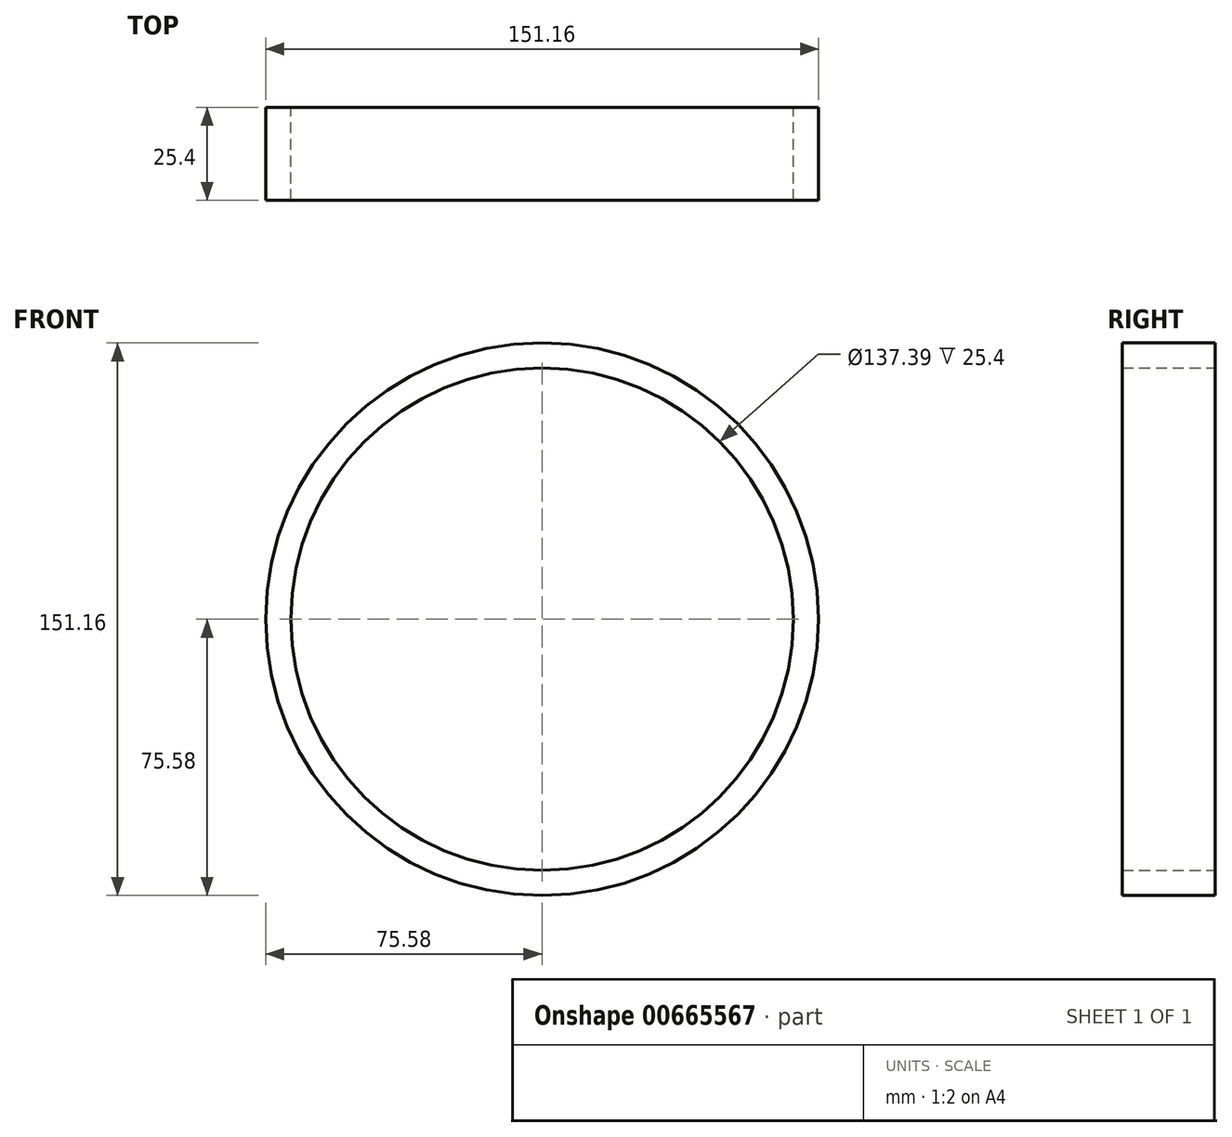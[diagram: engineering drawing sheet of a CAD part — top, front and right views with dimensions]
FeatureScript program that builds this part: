
annotation { "Feature Type Name" : "Feature", "Feature Type Description" : "" }
export const myFeature = defineFeature(function(context is Context, id is Id, definition is map)
    precondition{}
    {
        {
            var Q0;
            Q0=qCreatedBy(makeId("Front.planeOp"),FACE);
            var sketch = newSketch(context, id + "F0", { "sketchPlane" : qUnion([Q0])});
            skCircle(sketch, "E0", {"center": v(0, 0) * mm, "radius": 75.58 * mm});
            skSolve(sketch);
        }
        {
            var Q0;
            Q0=makeQuery(id+"F0.imprint","IMPRINT",FACE,{"disambiguationData":[TD([[makeQuery(id+"F0.imprint","IMPRINT",EDGE,{"derivedFrom":sQuery(id+"F0.wireOp",EDGE,"E0")}),1.0]])]});
            extrude(context, id + "F1", {"entities" : qUnion([Q0]), "endBound" : BoundingType.SYMMETRIC, "depth" : 25.4 * mm, "offsetDistance" : 25.4 * mm});
        }
        {
            var Q0;
            Q0=qCreatedBy(makeId("Front.planeOp"),FACE);
            var sketch = newSketch(context, id + "F2", { "sketchPlane" : qUnion([Q0])});
            skCircle(sketch, "E1", {"center": v(0, 0) * mm, "radius": 68.7 * mm});
            skSolve(sketch);
        }
        {
            var Q0;
            Q0 = qSketchRegion(id + "F2", true);
            extrude(context, id + "F3", {"entities" : qUnion([Q0]), "operationType" : NewBodyOperationType.REMOVE, "endBound" : BoundingType.SYMMETRIC, "depth" : 50.8 * mm, "offsetDistance" : 25.4 * mm});
        }
    });
